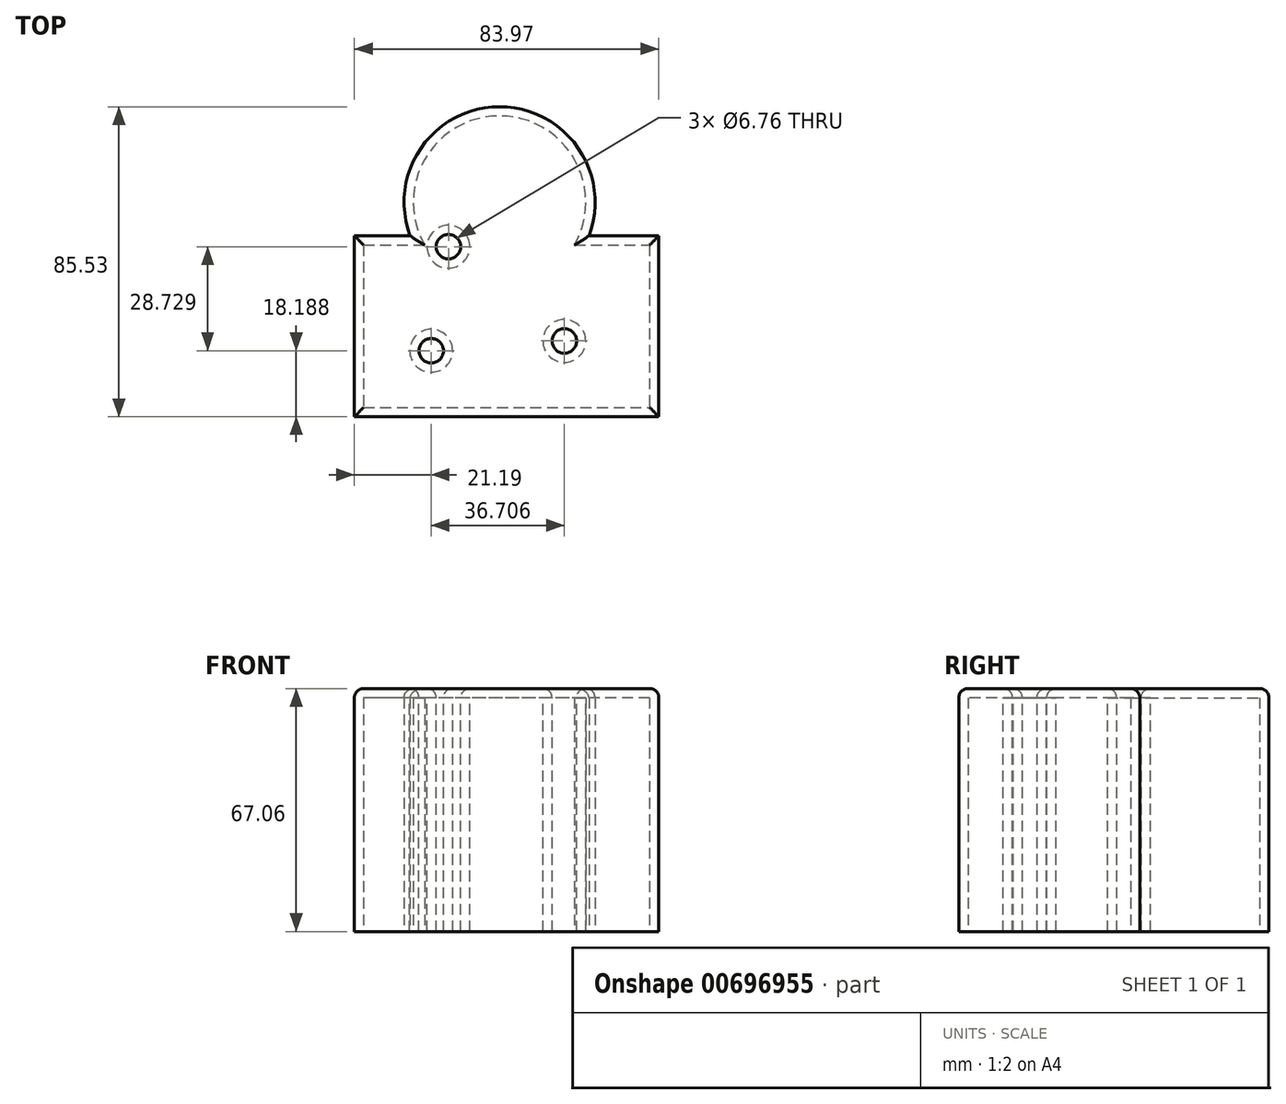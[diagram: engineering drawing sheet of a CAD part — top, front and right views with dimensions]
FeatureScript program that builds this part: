
annotation { "Feature Type Name" : "Feature", "Feature Type Description" : "" }
export const myFeature = defineFeature(function(context is Context, id is Id, definition is map)
    precondition{}
    {
        {
            var Q0;
            Q0=qCreatedBy(makeId("Top.planeOp"),FACE);
            var sketch = newSketch(context, id + "F0", { "sketchPlane" : qUnion([Q0])});
            skLineSegment(sketch, "E0.bottom", {"start": v(-35.1, 17.37) * mm, "end": v(-19.71, 17.37) * mm});
            skLineSegment(sketch, "E0.top", {"start": v(-35.1, -32.54) * mm, "end": v(48.86, -32.54) * mm});
            skLineSegment(sketch, "E0.left", {"start": v(-35.1, 17.37) * mm, "end": v(-35.1, -32.54) * mm});
            skLineSegment(sketch, "E0.right", {"start": v(48.86, 17.37) * mm, "end": v(48.86, -32.54) * mm});
            skArc(sketch, "E1", {"start": v(29.58, 17.37) * mm, "mid": v(4.93, 52.99) * mm, "end": v(-19.71, 17.37) * mm});
            skLineSegment(sketch, "E2.trimOffspring", {"start": v(29.58, 17.37) * mm, "end": v(48.86, 17.37) * mm});
            skSolve(sketch);
        }
        {
            var Q0;
            Q0=makeQuery(id+"F0.imprint","IMPRINT",FACE,{"disambiguationData":[TD([[makeQuery(id+"F0.imprint","IMPRINT",EDGE,{"derivedFrom":sQuery(id+"F0.wireOp",EDGE,"E0.bottom")}),-1.0]])]});
            extrude(context, id + "F1", {"entities" : qUnion([Q0]), "depth" : 67.06 * mm, "offsetDistance" : 25.4 * mm});
        }
        {
            var Q0;
            Q0=makeQuery(id+"F1.opExtrude","CAP_FACE",FACE,{"disambiguationData":[OSD([sQuery(id+"F0.wireOp",EDGE,"E0.bottom"),sQuery(id+"F0.wireOp",EDGE,"E0.top"),sQuery(id+"F0.wireOp",EDGE,"E0.left"),sQuery(id+"F0.wireOp",EDGE,"E0.right"),sQuery(id+"F0.wireOp",EDGE,"E1"),sQuery(id+"F0.wireOp",EDGE,"E2.trimOffspring")])],"isStart":false});
            var sketch = newSketch(context, id + "F2", { "sketchPlane" : qUnion([Q0])});
            skPoint(sketch, "E3", {"position": v(-9.16, 14.38) * mm});
            skPoint(sketch, "E4", {"position": v(-13.92, -14.35) * mm});
            skPoint(sketch, "E5", {"position": v(22.79, -11.64) * mm});
            skSolve(sketch);
        }
        {
            var Q0;
            Q0=sQuery(id+"F2.wireOp",VERTEX,"E3");
            var Q1;
            Q1=sQuery(id+"F2.wireOp",VERTEX,"E4");
            var Q2;
            Q2=sQuery(id+"F2.wireOp",VERTEX,"E5");
            var Q3;
            Q3=makeQuery(id+"F1.opExtrude","SWEPT_BODY",BODY,{"disambiguationData":[OSD([sQuery(id+"F0.wireOp",EDGE,"E0.bottom"),sQuery(id+"F0.wireOp",EDGE,"E0.top"),sQuery(id+"F0.wireOp",EDGE,"E0.left"),sQuery(id+"F0.wireOp",EDGE,"E0.right"),sQuery(id+"F0.wireOp",EDGE,"E1"),sQuery(id+"F0.wireOp",EDGE,"E2.trimOffspring")])]});
            hole(context, id + "F3", {"style" : HoleStyle.SIMPLE, "endStyle" : HoleEndStyle.THROUGH, "standardTappedOrClearance" : lookupTablePath({ "standard" : "ANSI", "fit" : "Normal (ASME)", "size" : "1/4", "type" : "Clearance" }), "standardBlindInLast" : lookupTablePath({ "fit" : "Free", "standard" : "ANSI", "size" : "1/4", "type" : "Clearance" }), "holeDiameter" : 6.76 * mm, "majorDiameter" : 6.35 * mm, "isTappedThrough" : true, "tappedDepth" : 12.7 * mm, "tapClearance" : 3, "locations" : qUnion([Q0, Q1, Q2]), "scope" : qUnion([Q3])});
        }
        {
            var Q0;
            Q0=makeQuery(id+"F1.opExtrude","CAP_EDGE",EDGE,{"disambiguationData":[OSD([sQuery(id+"F0.wireOp",EDGE,"E1")])],"isStart":false});
            var Q1;
            Q1=makeQuery(id+"F1.opExtrude","CAP_EDGE",EDGE,{"disambiguationData":[OSD([sQuery(id+"F0.wireOp",EDGE,"E0.left")])],"isStart":false});
            var Q2;
            Q2=makeQuery(id+"F1.opExtrude","CAP_FACE",FACE,{"disambiguationData":[OSD([sQuery(id+"F0.wireOp",EDGE,"E0.bottom"),sQuery(id+"F0.wireOp",EDGE,"E0.top"),sQuery(id+"F0.wireOp",EDGE,"E0.left"),sQuery(id+"F0.wireOp",EDGE,"E0.right"),sQuery(id+"F0.wireOp",EDGE,"E1"),sQuery(id+"F0.wireOp",EDGE,"E2.trimOffspring")])],"isStart":false});
            fillet(context, id + "F4", {"entities" : qUnion([Q0, Q1, Q2]), "radius" : 2.54 * mm, "tangentPropagation" : true, "allowEdgeOverflow" : false});
        }
        {
            var Q0;
            Q0=makeQuery(id+"F1.opExtrude","CAP_FACE",FACE,{"disambiguationData":[OSD([sQuery(id+"F0.wireOp",EDGE,"E0.bottom"),sQuery(id+"F0.wireOp",EDGE,"E0.top"),sQuery(id+"F0.wireOp",EDGE,"E0.left"),sQuery(id+"F0.wireOp",EDGE,"E0.right"),sQuery(id+"F0.wireOp",EDGE,"E1"),sQuery(id+"F0.wireOp",EDGE,"E2.trimOffspring")])],"isStart":true});
            shell(context, id + "F5", {"entities" : qUnion([Q0]), "thickness" : 2.54 * mm});
        }
    });
